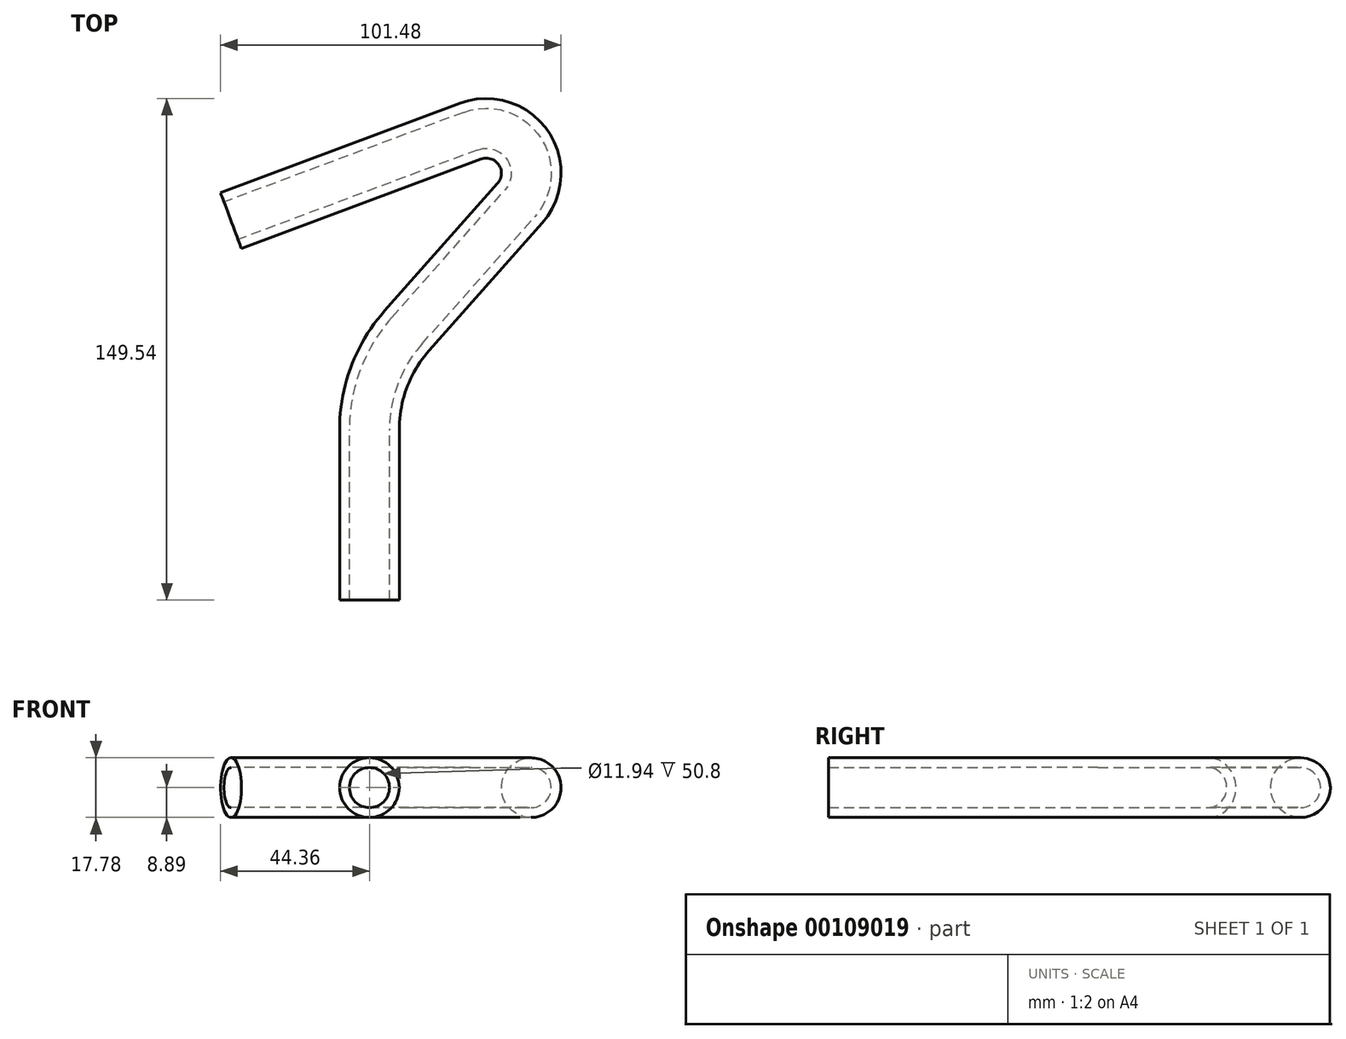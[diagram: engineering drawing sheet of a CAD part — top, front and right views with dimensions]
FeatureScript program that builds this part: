
annotation { "Feature Type Name" : "Feature", "Feature Type Description" : "" }
export const myFeature = defineFeature(function(context is Context, id is Id, definition is map)
    precondition{}
    {
        {
            var Q0;
            Q0=qCreatedBy(makeId("Top.planeOp"),FACE);
            var sketch = newSketch(context, id + "F0", { "sketchPlane" : qUnion([Q0])});
            skLineSegment(sketch, "E0", {"start": v(0, 0) * mm, "end": v(0, 50.8) * mm});
            skArc(sketch, "E1", {"start": v(0, 50.8) * mm, "mid": v(2.9, 66.58) * mm, "end": v(11.19, 80.32) * mm});
            skLineSegment(sketch, "E2", {"start": v(11.19, 80.32) * mm, "end": v(44.86, 118.35) * mm});
            skLineSegment(sketch, "E3", {"start": v(0, 50.8) * mm, "end": v(44.53, 50.8) * mm});
            skLineSegment(sketch, "E4", {"start": v(11.19, 80.32) * mm, "end": v(44.53, 50.8) * mm});
            skLineSegment(sketch, "E5", {"start": v(11.19, 80.32) * mm, "end": v(11.19, 50.8) * mm});
            skArc(sketch, "E6", {"start": v(44.86, 118.35) * mm, "mid": v(45.87, 134.83) * mm, "end": v(30.13, 139.8) * mm});
            skLineSegment(sketch, "E7", {"start": v(30.13, 139.8) * mm, "end": v(-41.24, 113.1) * mm});
            skSolve(sketch);
        }
        {
            var Q0;
            Q0=qCreatedBy(makeId("Front.planeOp"),FACE);
            var sketch = newSketch(context, id + "F1", { "sketchPlane" : qUnion([Q0])});
            skCircle(sketch, "E8", {"center": v(0, 0) * mm, "radius": 5.97 * mm});
            skCircle(sketch, "E9", {"center": v(0, 0) * mm, "radius": 8.9 * mm});
            skSolve(sketch);
        }
        {
            var Q0;
            Q0=makeQuery(id+"F1.imprint","IMPRINT",FACE,{"disambiguationData":[TD([[makeQuery(id+"F1.imprint","IMPRINT",EDGE,{"derivedFrom":sQuery(id+"F1.wireOp",EDGE,"E8")}),-1.0]])]});
            var Q1;
            Q1=sQuery(id+"F0.wireOp",EDGE,"E0");
            var Q2;
            Q2=sQuery(id+"F0.wireOp",EDGE,"E1");
            var Q3;
            Q3=sQuery(id+"F0.wireOp",EDGE,"E2");
            var Q4;
            Q4=sQuery(id+"F0.wireOp",EDGE,"E6");
            var Q5;
            Q5=sQuery(id+"F0.wireOp",EDGE,"E7");
            sweep(context, id + "F2", {"profiles" : qUnion([Q0]), "path" : qUnion([Q1, Q2, Q3, Q4, Q5])});
        }
    });
